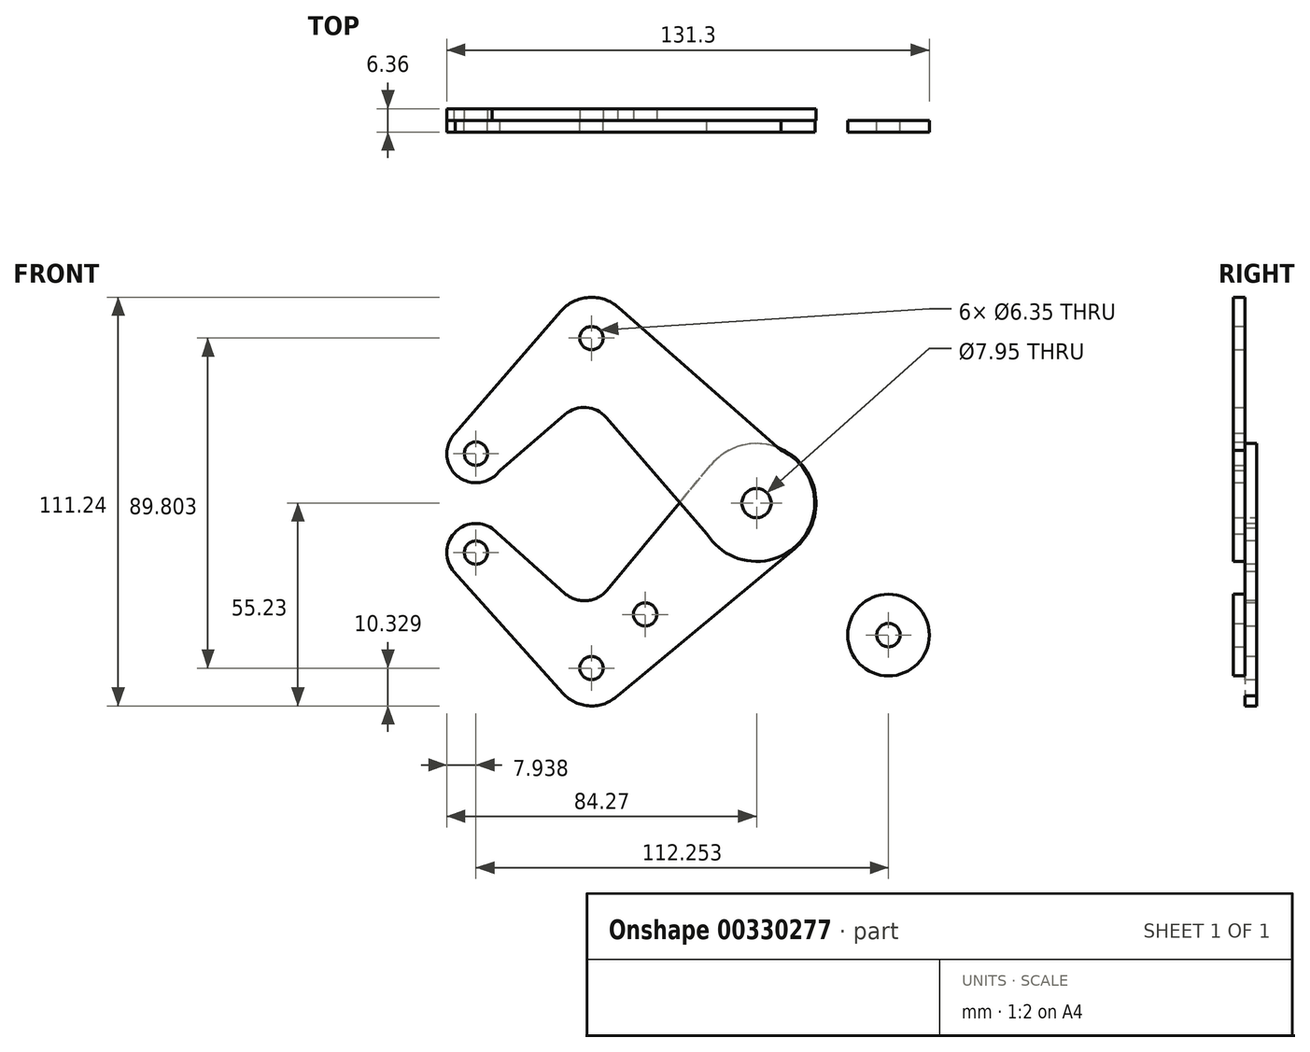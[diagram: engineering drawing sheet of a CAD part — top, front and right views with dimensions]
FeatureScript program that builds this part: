
annotation { "Feature Type Name" : "Feature", "Feature Type Description" : "" }
export const myFeature = defineFeature(function(context is Context, id is Id, definition is map)
    precondition{}
    {
        {
            var Q0;
            Q0=qCreatedBy(makeId("Front.planeOp"),FACE);
            var sketch = newSketch(context, id + "F0", { "sketchPlane" : qUnion([Q0])});
            skCircle(sketch, "E0", {"center": v(0, 0) * mm, "radius": 3.98 * mm});
            skCircle(sketch, "E1", {"center": v(0, 0) * mm, "radius": 15.88 * mm});
            skLineSegment(sketch, "E2", {"start": v(0, 0) * mm, "end": v(-44.9, 44.9) * mm});
            skLineSegment(sketch, "E3", {"start": v(0, 0) * mm, "end": v(35.92, -35.92) * mm});
            skCircle(sketch, "E4", {"center": v(35.92, -35.92) * mm, "radius": 11.11 * mm});
            skCircle(sketch, "E5", {"center": v(35.92, -35.92) * mm, "radius": 3.18 * mm});
            skLineSegment(sketch, "E6", {"start": v(28.06, -28.06) * mm, "end": v(25.82, -25.82) * mm});
            skLineSegment(sketch, "E7", {"start": v(25.82, -25.82) * mm, "end": v(28.06, -23.57) * mm});
            skCircle(sketch, "E8", {"center": v(28.06, -23.57) * mm, "radius": 3.18 * mm});
            skLineSegment(sketch, "E9", {"start": v(27.49, -43.15) * mm, "end": v(-10.08, -12.26) * mm});
            skLineSegment(sketch, "E10", {"start": v(14.14, 7.21) * mm, "end": v(44.42, -28.77) * mm});
            skCircle(sketch, "E11", {"center": v(-44.9, 44.9) * mm, "radius": 11.11 * mm});
            skCircle(sketch, "E12", {"center": v(-44.9, 44.9) * mm, "radius": 3.18 * mm});
            skLineSegment(sketch, "E13", {"start": v(-13.5, -8.36) * mm, "end": v(-40.9, 23.29) * mm});
            skLineSegment(sketch, "E14", {"start": v(6.69, 14.4) * mm, "end": v(-37.57, 53.25) * mm});
            skLineSegment(sketch, "E15", {"start": v(-44.9, 44.9) * mm, "end": v(-76.33, 13.47) * mm});
            skCircle(sketch, "E16", {"center": v(-76.33, 13.47) * mm, "radius": 7.94 * mm});
            skCircle(sketch, "E17", {"center": v(-76.33, 13.47) * mm, "radius": 3.18 * mm});
            skLineSegment(sketch, "E18", {"start": v(-81.97, 19.06) * mm, "end": v(-53.3, 52.17) * mm});
            skLineSegment(sketch, "E19", {"start": v(-69.84, 8.9) * mm, "end": v(-52.07, 24.12) * mm});
            skArc(sketch, "E20.filletArc", {"start": v(-40.9, 23.29) * mm, "mid": v(-46.31, 26.01) * mm, "end": v(-52.07, 24.12) * mm});
            skSolve(sketch);
        }
        {
            var Q0;
            {var subQ5=sQuery(id+"F0.wireOp",EDGE,"E13");Q0=makeQuery(id+"F0.imprint","IMPRINT",FACE,{"disambiguationData":[TD([[makeQuery(id+"F0.imprint","IMPRINT",EDGE,{"derivedFrom":subQ5}),-1.0]])]});}
            var Q1;
            {var subQ0=sQuery(id+"F0.wireOp",EDGE,"E18");Q1=makeQuery(id+"F0.imprint","IMPRINT",FACE,{"disambiguationData":[TD([[makeQuery(id+"F0.imprint","IMPRINT",EDGE,{"derivedFrom":subQ0}),-1.0]])]});}
            var Q2;
            {var subQ0=sQuery(id+"F0.wireOp",EDGE,"E11");var subQ1=sQuery(id+"F0.wireOp",EDGE,"E2");var subQ2=makeQuery(id+"F0.imprint","INTERSECT",VERTEX,{"derivedFrom":[subQ1,subQ0]});Q2=makeQuery(id+"F0.imprint","IMPRINT",FACE,{"disambiguationData":[TD([[makeQuery(id+"F0.imprint","IMPRINT",EDGE,{"disambiguationData":[TD([[subQ2,-1.0]])],"derivedFrom":subQ1}),1.0]])]});}
            var Q3;
            {var subQ0=sQuery(id+"F0.wireOp",EDGE,"E14");Q3=makeQuery(id+"F0.imprint","IMPRINT",FACE,{"disambiguationData":[TD([[makeQuery(id+"F0.imprint","IMPRINT",EDGE,{"derivedFrom":subQ0}),1.0]])]});}
            var Q4;
            {var subQ0=sQuery(id+"F0.wireOp",EDGE,"E11");var subQ2=sQuery(id+"F0.wireOp",EDGE,"E2");var subQ3=makeQuery(id+"F0.imprint","INTERSECT",VERTEX,{"derivedFrom":[subQ2,subQ0]});Q4=makeQuery(id+"F0.imprint","IMPRINT",FACE,{"disambiguationData":[TD([[makeQuery(id+"F0.imprint","IMPRINT",EDGE,{"disambiguationData":[TD([[subQ3,-1.0]])],"derivedFrom":subQ2}),-1.0]])]});}
            var Q5;
            Q5=makeQuery(id+"F0.imprint","IMPRINT",FACE,{"disambiguationData":[TD([[makeQuery(id+"F0.imprint","IMPRINT",EDGE,{"derivedFrom":sQuery(id+"F0.wireOp",EDGE,"E17")}),-1.0]])]});
            var Q6;
            {var subQ2=sQuery(id+"F0.wireOp",EDGE,"E2");var subQ5=sQuery(id+"F0.wireOp",EDGE,"E0");var subQ9=makeQuery(id+"F0.imprint","INTERSECT",VERTEX,{"derivedFrom":[subQ5,subQ2]});Q6=makeQuery(id+"F0.imprint","IMPRINT",FACE,{"disambiguationData":[TD([[makeQuery(id+"F0.imprint","IMPRINT",EDGE,{"disambiguationData":[TD([[subQ9,1.0]])],"derivedFrom":subQ5}),-1.0]])]});}
            var Q7;
            {var subQ5=sQuery(id+"F0.wireOp",EDGE,"E2");var subQ7=sQuery(id+"F0.wireOp",EDGE,"E0");var subQ8=makeQuery(id+"F0.imprint","INTERSECT",VERTEX,{"derivedFrom":[subQ7,subQ5]});Q7=makeQuery(id+"F0.imprint","IMPRINT",FACE,{"disambiguationData":[TD([[makeQuery(id+"F0.imprint","IMPRINT",EDGE,{"disambiguationData":[TD([[subQ8,-1.0]])],"derivedFrom":subQ7}),-1.0]])]});}
            var Q8;
            {var subQ0=sQuery(id+"F0.wireOp",EDGE,"E6");Q8=makeQuery(id+"F0.imprint","IMPRINT",FACE,{"disambiguationData":[TD([[makeQuery(id+"F0.imprint","IMPRINT",EDGE,{"derivedFrom":subQ0}),1.0]])]});}
            var Q9;
            {var subQ0=sQuery(id+"F0.wireOp",EDGE,"E6");Q9=makeQuery(id+"F0.imprint","IMPRINT",FACE,{"disambiguationData":[TD([[makeQuery(id+"F0.imprint","IMPRINT",EDGE,{"derivedFrom":subQ0}),-1.0]])]});}
            var Q10;
            Q10=makeQuery(id+"F0.imprint","IMPRINT",FACE,{"disambiguationData":[TD([[makeQuery(id+"F0.imprint","IMPRINT",EDGE,{"derivedFrom":sQuery(id+"F0.wireOp",EDGE,"E5")}),-1.0]])]});
            extrude(context, id + "F1", {"entities" : qUnion([Q0, Q1, Q2, Q3, Q4, Q5, Q6, Q7, Q8, Q9, Q10]), "depth" : 3.17 * mm});
        }
        {
            var Q0;
            Q0=qCreatedBy(makeId("Front.planeOp"),FACE);
            var sketch = newSketch(context, id + "F2", { "sketchPlane" : qUnion([Q0])});
            skArc(sketch, "E21", {"start": v(10.34, -12.46) * mm, "mid": v(11.45, 11.45) * mm, "end": v(-12.47, 10.33) * mm});
            skCircle(sketch, "E22", {"center": v(0, 0) * mm, "radius": 3.98 * mm});
            skLineSegment(sketch, "E23", {"start": v(0, 0) * mm, "end": v(-44.9, -44.9) * mm});
            skCircle(sketch, "E24", {"center": v(-44.9, -44.9) * mm, "radius": 10.33 * mm});
            skCircle(sketch, "E25", {"center": v(-44.9, -44.9) * mm, "radius": 3.18 * mm});
            skLineSegment(sketch, "E26", {"start": v(-44.9, -44.9) * mm, "end": v(-76.33, -13.47) * mm});
            skCircle(sketch, "E27", {"center": v(-76.33, -13.47) * mm, "radius": 7.94 * mm});
            skLineSegment(sketch, "E28", {"start": v(-82.3, -18.7) * mm, "end": v(-52.58, -51.8) * mm});
            skLineSegment(sketch, "E29", {"start": v(-71.9, -6.88) * mm, "end": v(-52.13, -24.58) * mm});
            skLineSegment(sketch, "E30", {"start": v(-40.7, -23.73) * mm, "end": v(-12.47, 10.33) * mm});
            skLineSegment(sketch, "E31", {"start": v(-37.8, -52.4) * mm, "end": v(10.34, -12.46) * mm});
            skLineSegment(sketch, "E32", {"start": v(-44.9, -44.9) * mm, "end": v(-30.3, -30.3) * mm});
            skCircle(sketch, "E33", {"center": v(-30.3, -30.3) * mm, "radius": 3.18 * mm});
            skCircle(sketch, "E34", {"center": v(-76.33, -13.47) * mm, "radius": 3.18 * mm});
            skArc(sketch, "E35.filletArc", {"start": v(-52.13, -24.58) * mm, "mid": v(-46.23, -26.58) * mm, "end": v(-40.7, -23.73) * mm});
            skSolve(sketch);
        }
        {
            var Q0;
            {var subQ13=sQuery(id+"F2.wireOp",EDGE,"E30");Q0=makeQuery(id+"F2.imprint","IMPRINT",FACE,{"disambiguationData":[TD([[makeQuery(id+"F2.imprint","IMPRINT",EDGE,{"derivedFrom":subQ13}),-1.0]])]});}
            var Q1;
            {var subQ0=sQuery(id+"F2.wireOp",EDGE,"E28");var subQ1=sQuery(id+"F2.wireOp",EDGE,"E24");var subQ2=makeQuery(id+"F2.imprint","INTERSECT",VERTEX,{"derivedFrom":[subQ1,subQ0]});Q1=makeQuery(id+"F2.imprint","IMPRINT",FACE,{"disambiguationData":[TD([[makeQuery(id+"F2.imprint","IMPRINT",EDGE,{"disambiguationData":[TD([[subQ2,1.0]])],"derivedFrom":subQ1}),-1.0]])]});}
            var Q2;
            {var subQ5=sQuery(id+"F2.wireOp",EDGE,"E24");var subQ8=makeQuery(id+"F2.imprint","INTERSECT",VERTEX,{"derivedFrom":[subQ5,sQuery(id+"F2.wireOp",EDGE,"E28")]});Q2=makeQuery(id+"F2.imprint","IMPRINT",FACE,{"disambiguationData":[TD([[makeQuery(id+"F2.imprint","IMPRINT",EDGE,{"disambiguationData":[TD([[subQ8,1.0]])],"derivedFrom":subQ5}),1.0]])]});}
            var Q3;
            {var subQ0=sQuery(id+"F2.wireOp",EDGE,"E26");var subQ1=sQuery(id+"F2.wireOp",EDGE,"E24");var subQ2=makeQuery(id+"F2.imprint","INTERSECT",VERTEX,{"derivedFrom":[subQ1,subQ0]});Q3=makeQuery(id+"F2.imprint","IMPRINT",FACE,{"disambiguationData":[TD([[makeQuery(id+"F2.imprint","IMPRINT",EDGE,{"disambiguationData":[TD([[subQ2,1.0]])],"derivedFrom":subQ1}),1.0]])]});}
            var Q4;
            {var subQ0=sQuery(id+"F2.wireOp",EDGE,"E31");Q4=makeQuery(id+"F2.imprint","IMPRINT",FACE,{"disambiguationData":[TD([[makeQuery(id+"F2.imprint","IMPRINT",EDGE,{"derivedFrom":subQ0}),1.0]])]});}
            var Q5;
            Q5=makeQuery(id+"F2.imprint","IMPRINT",FACE,{"disambiguationData":[TD([[makeQuery(id+"F2.imprint","IMPRINT",EDGE,{"derivedFrom":sQuery(id+"F2.wireOp",EDGE,"E34")}),-1.0]])]});
            extrude(context, id + "F3", {"entities" : qUnion([Q0, Q1, Q2, Q3, Q4, Q5]), "operationType" : NewBodyOperationType.ADD, "oppositeDirection" : true, "depth" : 3.17 * mm});
        }
    });
